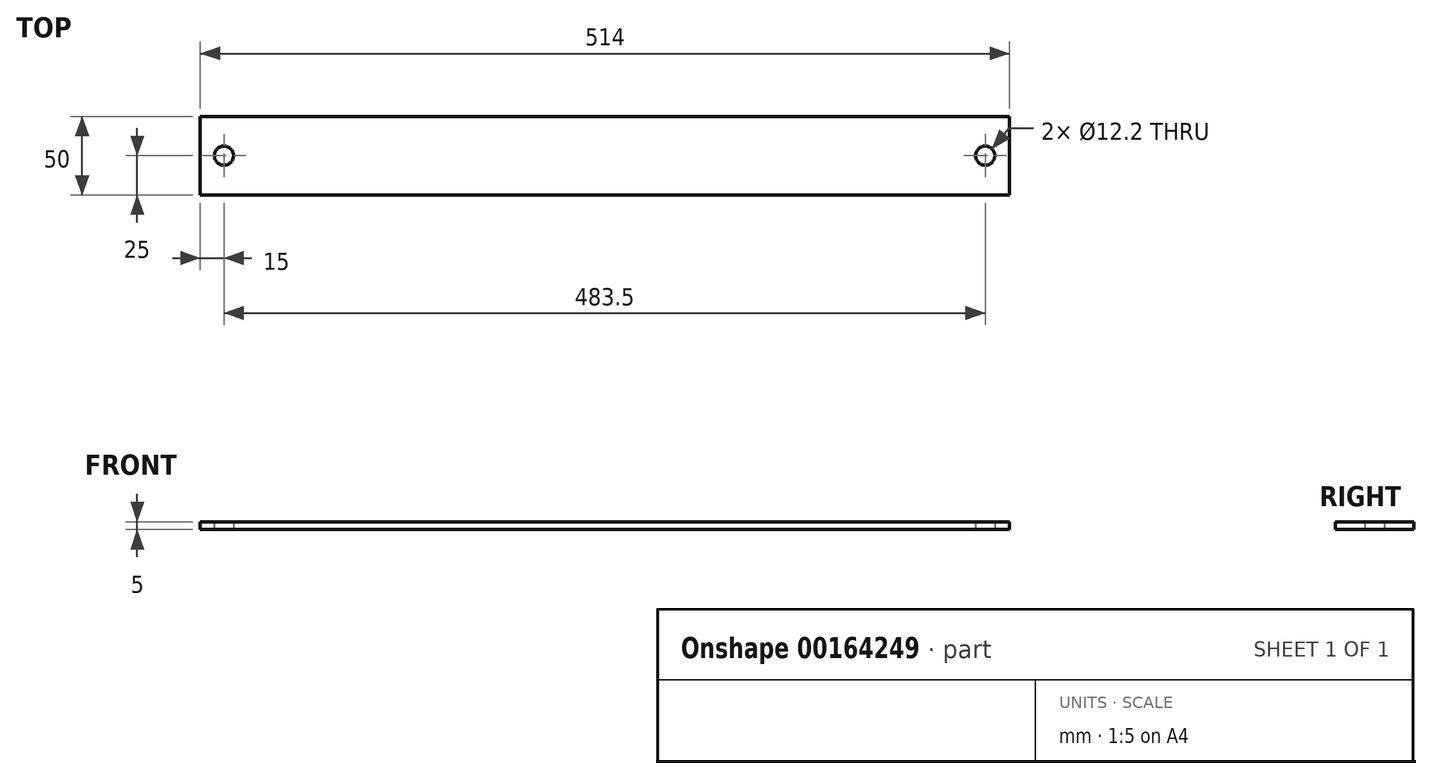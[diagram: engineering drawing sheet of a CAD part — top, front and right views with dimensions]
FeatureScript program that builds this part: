
annotation { "Feature Type Name" : "Feature", "Feature Type Description" : "" }
export const myFeature = defineFeature(function(context is Context, id is Id, definition is map)
    precondition{}
    {
        {
            var Q0;
            Q0=qCreatedBy(makeId("Top.planeOp"),FACE);
            var sketch = newSketch(context, id + "F0", { "sketchPlane" : qUnion([Q0])});
            skLineSegment(sketch, "E0.bottom", {"start": v(10.82, 0) * mm, "end": v(524.82, 0) * mm});
            skLineSegment(sketch, "E0.top", {"start": v(10.82, 50) * mm, "end": v(524.82, 50) * mm});
            skLineSegment(sketch, "E0.left", {"start": v(10.82, 0) * mm, "end": v(10.82, 50) * mm});
            skLineSegment(sketch, "E0.right", {"start": v(524.82, 0) * mm, "end": v(524.82, 50) * mm});
            skCircle(sketch, "E1", {"center": v(25.82, 25) * mm, "radius": 6.1 * mm});
            skCircle(sketch, "E2", {"center": v(509.32, 25) * mm, "radius": 6.1 * mm});
            skSolve(sketch);
        }
        {
            var Q0;
            Q0 = qSketchRegion(id + "F0", true);
            extrude(context, id + "F1", {"entities" : qUnion([Q0]), "depth" : 5 * mm});
        }
    });
